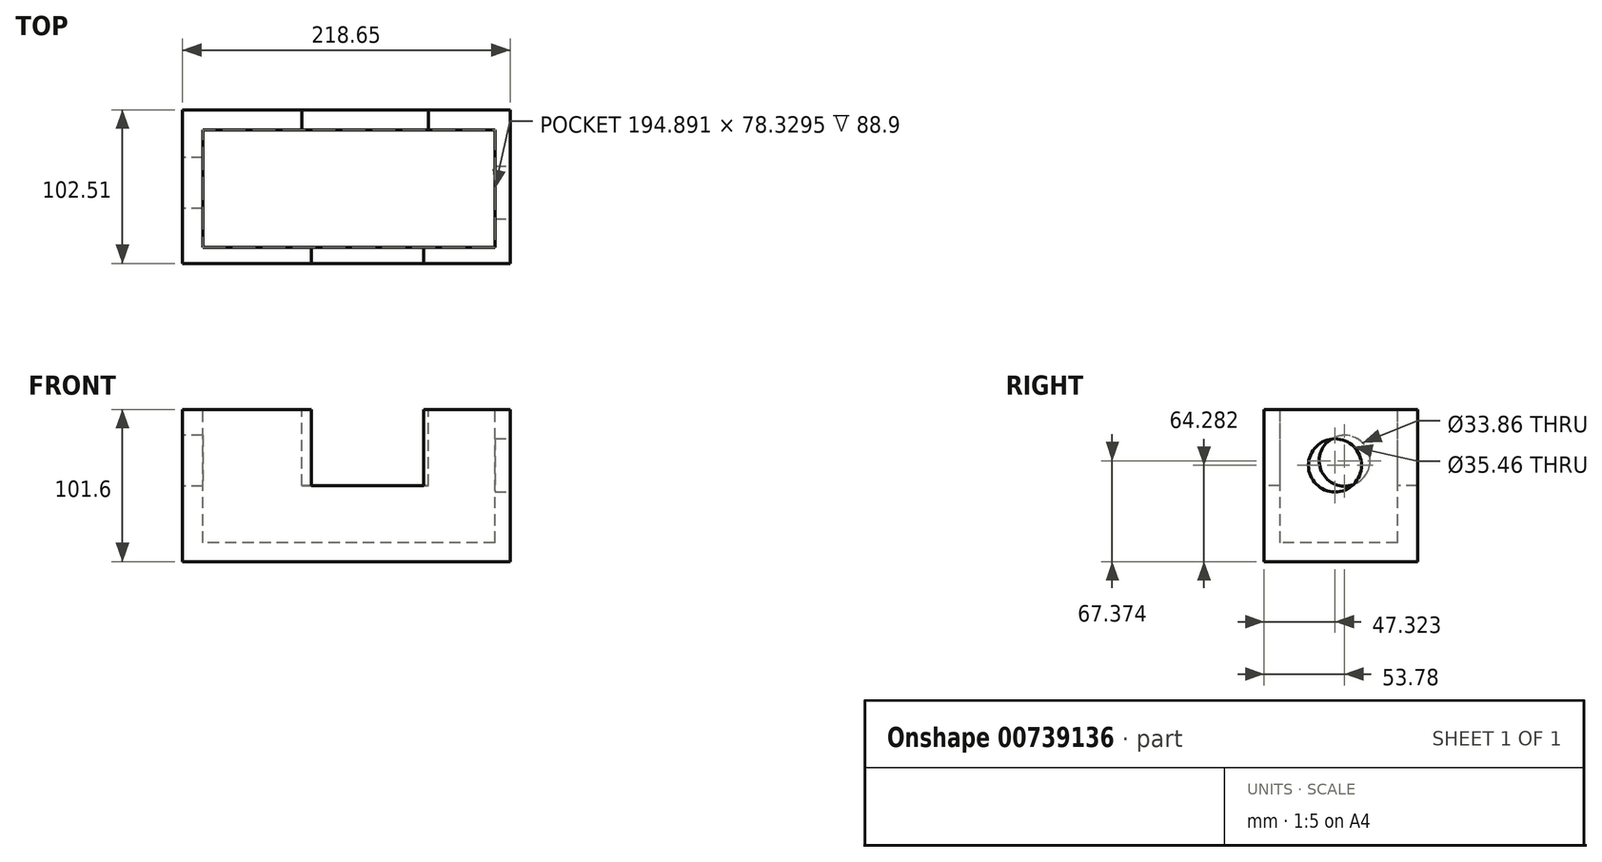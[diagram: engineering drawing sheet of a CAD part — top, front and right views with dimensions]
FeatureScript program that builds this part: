
annotation { "Feature Type Name" : "Feature", "Feature Type Description" : "" }
export const myFeature = defineFeature(function(context is Context, id is Id, definition is map)
    precondition{}
    {
        {
            var Q0;
            Q0=qCreatedBy(makeId("Top.planeOp"),FACE);
            var sketch = newSketch(context, id + "F0", { "sketchPlane" : qUnion([Q0])});
            skLineSegment(sketch, "E0.bottom", {"start": v(-109.51, 48.73) * mm, "end": v(109.14, 48.73) * mm});
            skLineSegment(sketch, "E0.top", {"start": v(-109.51, -53.78) * mm, "end": v(109.14, -53.78) * mm});
            skLineSegment(sketch, "E0.left", {"start": v(-109.51, 48.73) * mm, "end": v(-109.51, -53.78) * mm});
            skLineSegment(sketch, "E0.right", {"start": v(109.14, 48.73) * mm, "end": v(109.14, -53.78) * mm});
            skSolve(sketch);
        }
        {
            var Q0;
            Q0 = qSketchRegion(id + "F0", true);
            var Q1;
            Q1=makeQuery(id+"F0.imprint","IMPRINT",FACE,{"disambiguationData":[TD([[makeQuery(id+"F0.imprint","IMPRINT",EDGE,{"derivedFrom":sQuery(id+"F0.wireOp",EDGE,"E0.bottom")}),-1.0]])]});
            extrude(context, id + "F1", {"entities" : qUnion([Q0, Q1]), "depth" : 101.6 * mm, "offsetDistance" : 25.4 * mm});
        }
        {
            var Q0;
            Q0=makeQuery(id+"F1.opExtrude","CAP_FACE",FACE,{"disambiguationData":[OSD([sQuery(id+"F0.wireOp",EDGE,"E0.bottom"),sQuery(id+"F0.wireOp",EDGE,"E0.top"),sQuery(id+"F0.wireOp",EDGE,"E0.left"),sQuery(id+"F0.wireOp",EDGE,"E0.right")])],"isStart":false});
            var sketch = newSketch(context, id + "F2", { "sketchPlane" : qUnion([Q0])});
            skLineSegment(sketch, "E1.bottom", {"start": v(98.9, 35.3) * mm, "end": v(-95.99, 35.3) * mm});
            skLineSegment(sketch, "E1.top", {"start": v(98.9, -43.03) * mm, "end": v(-95.99, -43.03) * mm});
            skLineSegment(sketch, "E1.left", {"start": v(98.9, 35.3) * mm, "end": v(98.9, -43.03) * mm});
            skLineSegment(sketch, "E1.right", {"start": v(-95.99, 35.3) * mm, "end": v(-95.99, -43.03) * mm});
            skSolve(sketch);
        }
        {
            var Q0;
            Q0 = qSketchRegion(id + "F2", true);
            var Q1;
            Q1=makeQuery(id+"F2.imprint","IMPRINT",FACE,{"disambiguationData":[TD([[makeQuery(id+"F2.imprint","IMPRINT",EDGE,{"derivedFrom":sQuery(id+"F2.wireOp",EDGE,"E1.bottom")}),1.0]])]});
            extrude(context, id + "F3", {"entities" : qUnion([Q0, Q1]), "operationType" : NewBodyOperationType.REMOVE, "oppositeDirection" : true, "depth" : 88.9 * mm, "offsetDistance" : 25.4 * mm});
        }
        {
            var Q0;
            Q0=makeQuery(id+"F1.opExtrude","CAP_FACE",FACE,{"disambiguationData":[OSD([sQuery(id+"F0.wireOp",EDGE,"E0.bottom"),sQuery(id+"F0.wireOp",EDGE,"E0.top"),sQuery(id+"F0.wireOp",EDGE,"E0.left"),sQuery(id+"F0.wireOp",EDGE,"E0.right")])],"isStart":false});
            var sketch = newSketch(context, id + "F4", { "sketchPlane" : qUnion([Q0])});
            skLineSegment(sketch, "E2", {"start": v(54.69, 48.73) * mm, "end": v(54.69, 35.3) * mm});
            skLineSegment(sketch, "E3", {"start": v(-29.74, 48.73) * mm, "end": v(-29.74, 35.3) * mm});
            skLineSegment(sketch, "E4", {"start": v(51.47, -43.03) * mm, "end": v(51.47, -53.78) * mm});
            skLineSegment(sketch, "E5", {"start": v(-23.53, -43.03) * mm, "end": v(-23.53, -53.78) * mm});
            skSolve(sketch);
        }
        {
            var Q0;
            Q0 = qSketchRegion(id + "F4", true);
            var Q1;
            {var subQ0=sQuery(id+"F4.wireOp",EDGE,"E2");Q1=makeQuery(id+"F4.imprint","IMPRINT",FACE,{"disambiguationData":[TD([[makeQuery(id+"F4.imprint","IMPRINT",EDGE,{"derivedFrom":subQ0}),-1.0]])]});}
            var Q2;
            {var subQ0=sQuery(id+"F4.wireOp",EDGE,"E4");Q2=makeQuery(id+"F4.imprint","IMPRINT",FACE,{"disambiguationData":[TD([[makeQuery(id+"F4.imprint","IMPRINT",EDGE,{"derivedFrom":subQ0}),-1.0]])]});}
            extrude(context, id + "F5", {"entities" : qUnion([Q0, Q1, Q2]), "operationType" : NewBodyOperationType.REMOVE, "oppositeDirection" : true, "depth" : 50.8 * mm, "offsetDistance" : 25.4 * mm});
        }
        {
            var Q0;
            Q0=makeQuery(id+"F1.opExtrude","SWEPT_FACE",FACE,{"disambiguationData":[OSD([sQuery(id+"F0.wireOp",EDGE,"E0.left")])]});
            var sketch = newSketch(context, id + "F6", { "sketchPlane" : qUnion([Q0])});
            skCircle(sketch, "E6", {"center": v(0, 67.37) * mm, "radius": 16.93 * mm});
            skSolve(sketch);
        }
        {
            var Q0;
            Q0 = qSketchRegion(id + "F6", true);
            var Q1;
            Q1=makeQuery(id+"F6.imprint","IMPRINT",FACE,{"disambiguationData":[TD([[makeQuery(id+"F6.imprint","IMPRINT",EDGE,{"derivedFrom":sQuery(id+"F6.wireOp",EDGE,"E6")}),1.0]])]});
            extrude(context, id + "F7", {"entities" : qUnion([Q0, Q1]), "operationType" : NewBodyOperationType.REMOVE, "oppositeDirection" : true, "depth" : 25.4 * mm, "offsetDistance" : 25.4 * mm});
        }
        {
            var Q0;
            Q0=makeQuery(id+"F1.opExtrude","SWEPT_FACE",FACE,{"disambiguationData":[OSD([sQuery(id+"F0.wireOp",EDGE,"E0.right")])]});
            var sketch = newSketch(context, id + "F8", { "sketchPlane" : qUnion([Q0])});
            skCircle(sketch, "E7", {"center": v(-6.46, 64.28) * mm, "radius": 17.73 * mm});
            skSolve(sketch);
        }
        {
            var Q0;
            Q0=makeQuery(id+"F8.imprint","IMPRINT",FACE,{"disambiguationData":[TD([[makeQuery(id+"F8.imprint","IMPRINT",EDGE,{"derivedFrom":sQuery(id+"F8.wireOp",EDGE,"E7")}),1.0]])]});
            extrude(context, id + "F9", {"entities" : qUnion([Q0]), "operationType" : NewBodyOperationType.REMOVE, "oppositeDirection" : true, "depth" : 25.4 * mm, "offsetDistance" : 25.4 * mm});
        }
    });
